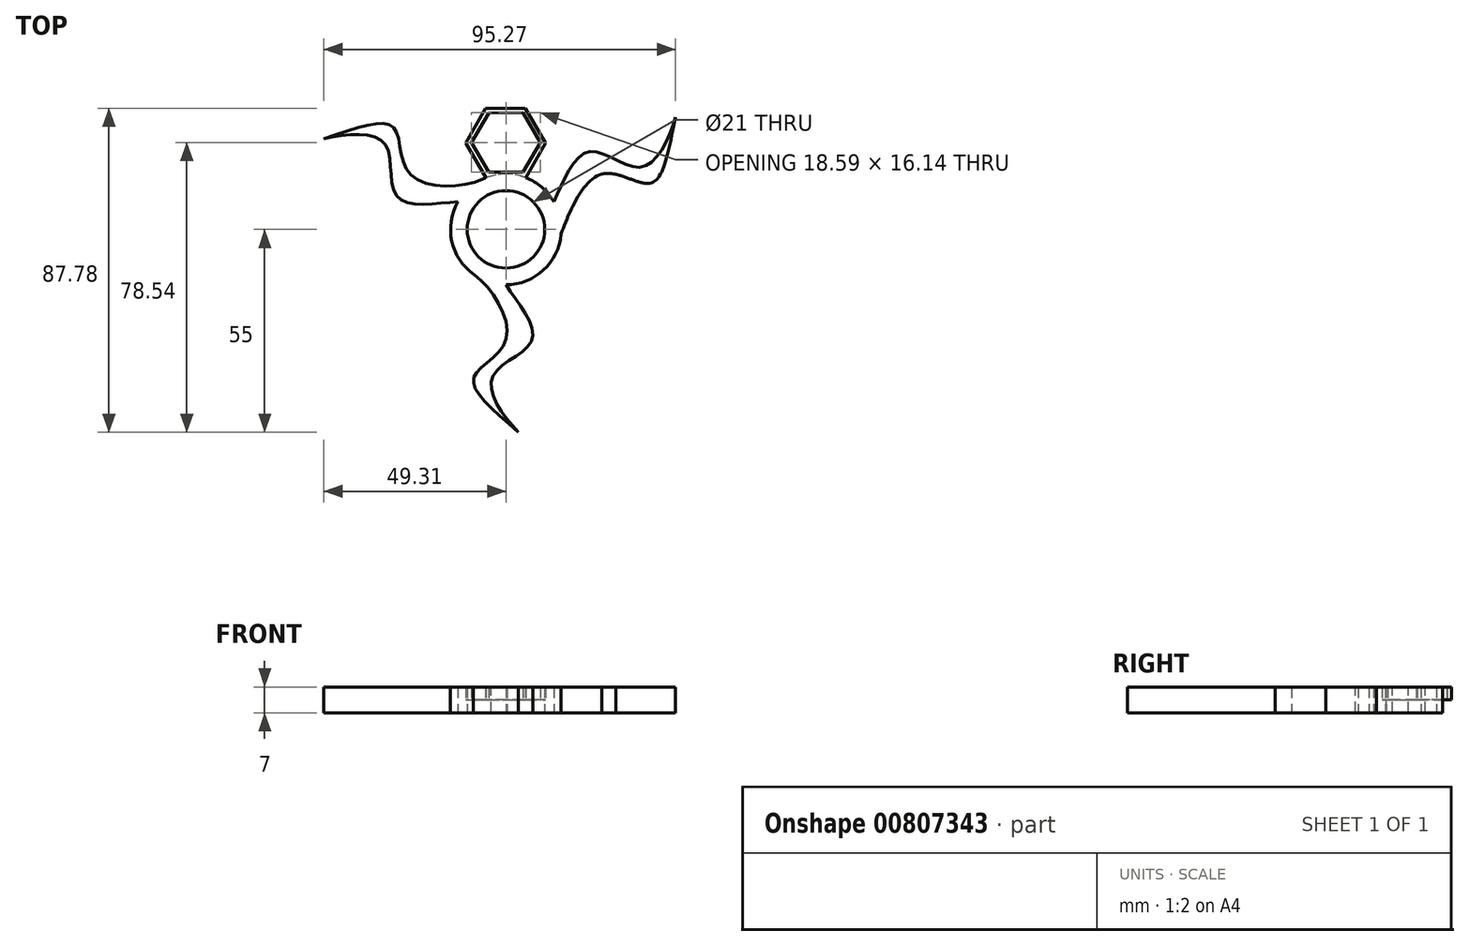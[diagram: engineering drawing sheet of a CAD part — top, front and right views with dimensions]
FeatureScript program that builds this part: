
annotation { "Feature Type Name" : "Feature", "Feature Type Description" : "" }
export const myFeature = defineFeature(function(context is Context, id is Id, definition is map)
    precondition{}
    {
        {
            var Q0;
            Q0=qCreatedBy(makeId("Top.planeOp"),FACE);
            var sketch = newSketch(context, id + "F0", { "sketchPlane" : qUnion([Q0])});
            skCircle(sketch, "E0", {"center": v(0, 0) * mm, "radius": 15 * mm});
            skLineSegment(sketch, "E1", {"start": v(0, 0) * mm, "end": v(0, -58.65) * mm, "construction": true});
            skLineSegment(sketch, "E2", {"start": v(0, 0) * mm, "end": v(37.98, 21.93) * mm, "construction": true});
            skLineSegment(sketch, "E3", {"start": v(0, 0) * mm, "end": v(-36.56, 21.1) * mm, "construction": true});
            skFitSpline(sketch, "E4.MirrorCS", {"points": [v(-6.36, 13.59) * mm, v(-25.98, 15) * mm, v(-30.32, 27.48) * mm, v(-49.3, 24.6) * mm], "startDerivative": vector(-45.6, -21.34) * mm, "endDerivative": vector(-78.42, -25.07) * mm});
            skFitSpline(sketch, "E5.MirrorCS", {"points": [v(-13, 7.5) * mm, v(-29.48, 8.94) * mm, v(-32.82, 23.15) * mm, v(-49.3, 24.6) * mm], "startDerivative": vector(-48.5, -3.02) * mm, "endDerivative": vector(-50.92, -11.46) * mm});
            skFitSpline(sketch, "E6.MirrorCS", {"points": [v(13, 7.5) * mm, v(22.48, 21.06) * mm, v(36.46, 16.85) * mm, v(45.96, 30.4) * mm], "startDerivative": vector(21.64, 43.51) * mm, "endDerivative": vector(15.53, 49.83) * mm});
            skFitSpline(sketch, "E7.MirrorCS", {"points": [v(14.94, -1.29) * mm, v(25.98, 15) * mm, v(38.96, 12.52) * mm, v(45.96, 30.4) * mm], "startDerivative": vector(17.11, 47.34) * mm, "endDerivative": vector(17.5, 80.45) * mm});
            skCircle(sketch, "E8", {"center": v(0, 0) * mm, "radius": 10.5 * mm});
            skPoint(sketch, "E9", {"position": v(6.98, 25.09) * mm});
            skPoint(sketch, "E10.orphan", {"position": v(4.9, 25.73) * mm});
            skPoint(sketch, "E11", {"position": v(2.09, 25.11) * mm});
            skFitSpline(sketch, "E12.MirrorCS", {"points": [v(13, 7.5) * mm, v(22.48, 21.06) * mm, v(36.46, 16.85) * mm, v(45.96, 30.4) * mm], "startDerivative": vector(21.64, 43.51) * mm, "endDerivative": vector(15.53, 49.83) * mm});
            skFitSpline(sketch, "E13.MirrorCS", {"points": [v(14.94, -1.29) * mm, v(25.98, 15) * mm, v(38.96, 12.52) * mm, v(45.96, 30.4) * mm], "startDerivative": vector(4.31, 50.15) * mm, "endDerivative": vector(17.5, 80.45) * mm});
            skLineSegment(sketch, "E14.MirrorCS", {"start": v(0, 0) * mm, "end": v(0, -43.85) * mm, "construction": true});
            skFitSpline(sketch, "E15.MirrorCS", {"points": [v(-6.36, 13.59) * mm, v(-25.98, 15) * mm, v(-30.32, 27.48) * mm, v(-49.3, 24.6) * mm], "startDerivative": vector(-45.6, -21.34) * mm, "endDerivative": vector(-78.42, -25.07) * mm});
            skFitSpline(sketch, "E16.MirrorCS", {"points": [v(-8.59, -12.3) * mm, v(0, -30) * mm, v(-8.64, -40) * mm, v(3.35, -55) * mm], "startDerivative": vector(41.28, -28.81) * mm, "endDerivative": vector(60.92, -55.38) * mm});
            skFitSpline(sketch, "E17.MirrorCS", {"points": [v(0, -15) * mm, v(7, -30) * mm, v(-3.64, -40) * mm, v(3.35, -55) * mm], "startDerivative": vector(26.87, -40.5) * mm, "endDerivative": vector(35.39, -38.37) * mm});
            skPoint(sketch, "E18.1.internal.orphan", {"position": v(-7, -30) * mm});
            skPoint(sketch, "E18.2.internal.orphan", {"position": v(3.64, -40) * mm});
            skPoint(sketch, "E19.0.internal.orphan", {"position": v(8.59, -12.3) * mm});
            skPoint(sketch, "E19.2.internal.orphan", {"position": v(8.64, -40) * mm});
            skPoint(sketch, "E20.orphan", {"position": v(-3.35, -55) * mm});
            skPoint(sketch, "E21.endSnap0", {"position": v(0, -21.93) * mm});
            skSolve(sketch);
        }
        {
            var Q0;
            Q0=qSketchRegion(id+"F0",true);
            extrude(context, id + "F1", {"entities" : qUnion([Q0]), "endBound" : BoundingType.SYMMETRIC, "depth" : 7 * mm, "offsetDistance" : 25 * mm});
        }
        {
            var Q0;
            Q0=qCreatedBy(makeId("Top.planeOp"),FACE);
            var sketch = newSketch(context, id + "F2", { "sketchPlane" : qUnion([Q0])});
            skPoint(sketch, "E22.orphan", {"position": v(11.47, 6.62) * mm});
            skLineSegment(sketch, "E23.0", {"start": v(9.3, 23.58) * mm, "end": v(4.68, 15.5) * mm});
            skLineSegment(sketch, "E23.1", {"start": v(4.68, 15.5) * mm, "end": v(-4.62, 15.47) * mm});
            skLineSegment(sketch, "E23.2", {"start": v(-4.62, 15.47) * mm, "end": v(-9.3, 23.5) * mm});
            skLineSegment(sketch, "E23.3", {"start": v(-9.3, 23.5) * mm, "end": v(-4.68, 31.57) * mm});
            skLineSegment(sketch, "E23.4", {"start": v(-4.68, 31.57) * mm, "end": v(4.62, 31.6) * mm});
            skLineSegment(sketch, "E23.5", {"start": v(4.62, 31.6) * mm, "end": v(9.3, 23.58) * mm});
            skPoint(sketch, "E23.0.midPoint", {"position": v(6.99, 19.54) * mm});
            skLineSegment(sketch, "E24.0", {"start": v(-5.46, 13.97) * mm, "end": v(-10.91, 23.34) * mm});
            skLineSegment(sketch, "E24.1", {"start": v(-10.91, 23.34) * mm, "end": v(-5.53, 32.74) * mm});
            skLineSegment(sketch, "E24.2", {"start": v(-5.53, 32.74) * mm, "end": v(5.3, 32.78) * mm});
            skLineSegment(sketch, "E24.3", {"start": v(5.3, 32.78) * mm, "end": v(10.76, 23.42) * mm});
            skLineSegment(sketch, "E24.4", {"start": v(10.76, 23.42) * mm, "end": v(5.39, 14) * mm});
            skLineSegment(sketch, "E24.5", {"start": v(5.39, 14) * mm, "end": v(-5.46, 13.97) * mm});
            skPoint(sketch, "E24.0.midPoint", {"position": v(-8.18, 18.65) * mm});
            skPoint(sketch, "E23.cCircle.center.orphan", {"position": v(0, 23.54) * mm});
            skSolve(sketch);
        }
        {
            var Q0;
            Q0 = qSketchRegion(id + "F2", true);
            var Q1;
            Q1=makeQuery(id+"F1.opExtrude","CAP_FACE",FACE,{"disambiguationData":[OSD([sQuery(id+"F0.wireOp",EDGE,"E4.MirrorCS"),sQuery(id+"F0.wireOp",EDGE,"E5.MirrorCS"),sQuery(id+"F0.wireOp",EDGE,"E7.MirrorCS"),sQuery(id+"F0.wireOp",EDGE,"E8"),sQuery(id+"F0.wireOp",EDGE,"E12.MirrorCS"),sQuery(id+"F0.wireOp",EDGE,"E13.MirrorCS"),sQuery(id+"F0.wireOp",EDGE,"E15.MirrorCS"),sQuery(id+"F0.wireOp",EDGE,"E16.MirrorCS"),sQuery(id+"F0.wireOp",EDGE,"E17.MirrorCS"),sQuery(id+"F0.wireOp",EDGE,"E0")])],"isStart":false});
            extrude(context, id + "F3", {"entities" : qUnion([Q0]), "operationType" : NewBodyOperationType.ADD, "endBound" : BoundingType.UP_TO_SURFACE, "depth" : 3.5 * mm, "endBoundEntityFace" : qUnion([Q1]), "offsetDistance" : 25 * mm});
        }
    });
